# Revit family: Storage-Freestanding-Teknion-JNFBPL-Beam_Tower_Lateral-R20161
name_source: partatom
category: Furniture
revit_build: Autodesk Revit Architecture 2016 (Build: 20150220_1215(x64)
units: mm (PartAtom-declared; Revit-internal decimal feet)

## family parameters
Always vertical = Yes
Cut with Voids When Loaded = No
OmniClass Number = 23.40.20.00
OmniClass Title = General Furniture and Specialties
Room Calculation Point = No
Shared = Yes
Work Plane-Based = No

## types (2) — shared parameters
Assembly Code = E2020200
Manufacturer = Teknion
Manufacturer Fax = 416.661.4586
Part Number = JNFBPL
Product Documentation Link = http://www.teknion.com
Product Line = Expansion Cityline
Product Page URL = http://www.teknion.com
Series = Expansion Cityline
Sustainability Data = http://www.teknion.com
URL = www.teknion.com
Unit Weight URL = http://www.teknion.com
Warranty = http://www.teknion.com
Width = 15 "

## per-type parameters (varying)
| type | Box, Box File Drawer Configuration | Description | File, File Drawer Configuration | Model |
| Solid - Box, Box, File Drawer Configuration | Yes | Beam Tower with Drawers – Lateral Access, Solid, Box, Box File Drawer Configuration | No | JNFBPLSF |
| Solid - File, File, Drawer Configuration | No | Beam Tower with Drawers – Lateral Access, Solid, File, File, Drawer Configuration | Yes | JNFBPLSB |

## geometry (parser evidence)
native form markers: Blend x2, Sweep x1
no freeform markers — native parametric forms only
